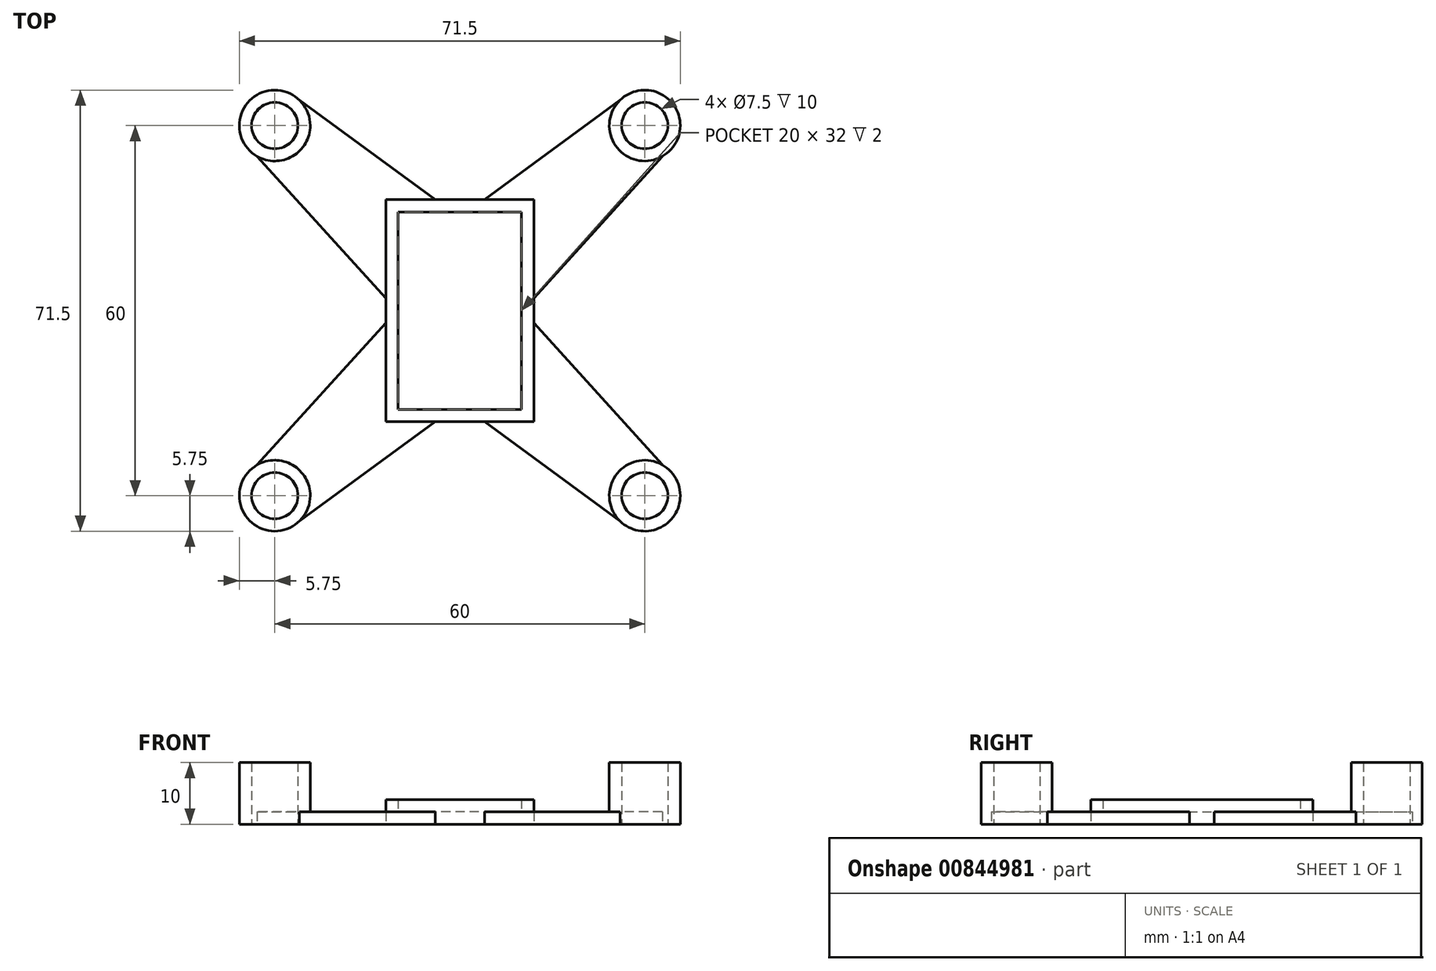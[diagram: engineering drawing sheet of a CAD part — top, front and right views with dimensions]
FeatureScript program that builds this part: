
annotation { "Feature Type Name" : "Feature", "Feature Type Description" : "" }
export const myFeature = defineFeature(function(context is Context, id is Id, definition is map)
    precondition{}
    {
        {
            var Q0;
            Q0=qCreatedBy(makeId("Top.planeOp"),FACE);
            var sketch = newSketch(context, id + "F0", { "sketchPlane" : qUnion([Q0])});
            skLineSegment(sketch, "E0.bottom", {"start": v(-30, 30) * mm, "end": v(30, 30) * mm, "construction": true});
            skLineSegment(sketch, "E0.top", {"start": v(-30, -30) * mm, "end": v(30, -30) * mm, "construction": true});
            skLineSegment(sketch, "E0.left", {"start": v(-30, 30) * mm, "end": v(-30, -30) * mm, "construction": true});
            skLineSegment(sketch, "E0.right", {"start": v(30, 30) * mm, "end": v(30, -30) * mm, "construction": true});
            skPoint(sketch, "E0.middle", {"position": v(0, 0) * mm});
            skCircle(sketch, "E1", {"center": v(-30, 30) * mm, "radius": 3.75 * mm});
            skCircle(sketch, "E2", {"center": v(30, 30) * mm, "radius": 3.75 * mm});
            skCircle(sketch, "E3", {"center": v(30, -30) * mm, "radius": 3.75 * mm});
            skCircle(sketch, "E4", {"center": v(-30, -30) * mm, "radius": 3.75 * mm});
            skLineSegment(sketch, "E5.bottom", {"start": v(-12, 18) * mm, "end": v(12, 18) * mm});
            skLineSegment(sketch, "E5.top", {"start": v(-12, -18) * mm, "end": v(12, -18) * mm});
            skLineSegment(sketch, "E5.left", {"start": v(-12, 18) * mm, "end": v(-12, -18) * mm});
            skLineSegment(sketch, "E5.right", {"start": v(12, 18) * mm, "end": v(12, -18) * mm});
            skCircle(sketch, "E6", {"center": v(-30, 30) * mm, "radius": 5.75 * mm});
            skLineSegment(sketch, "E7.bottom", {"start": v(-10, 16) * mm, "end": v(10, 16) * mm});
            skLineSegment(sketch, "E7.top", {"start": v(-10, -16) * mm, "end": v(10, -16) * mm});
            skLineSegment(sketch, "E7.left", {"start": v(-10, 16) * mm, "end": v(-10, -16) * mm});
            skLineSegment(sketch, "E7.right", {"start": v(10, 16) * mm, "end": v(10, -16) * mm});
            skCircle(sketch, "E8", {"center": v(-30, -30) * mm, "radius": 5.75 * mm});
            skCircle(sketch, "E9", {"center": v(30, -30) * mm, "radius": 5.75 * mm});
            skCircle(sketch, "E10", {"center": v(30, 30) * mm, "radius": 5.75 * mm});
            skLineSegment(sketch, "E11", {"start": v(-4, 18) * mm, "end": v(-26, 34.13) * mm});
            skLineSegment(sketch, "E12", {"start": v(-32.84, 25) * mm, "end": v(-12, 2) * mm});
            skLineSegment(sketch, "E13.MirrorCS", {"start": v(4, 18) * mm, "end": v(26, 34.13) * mm});
            skLineSegment(sketch, "E14.MirrorCS", {"start": v(32.84, 25) * mm, "end": v(12, 2) * mm});
            skLineSegment(sketch, "E15.MirrorCS", {"start": v(32.84, -25) * mm, "end": v(12, -2) * mm});
            skLineSegment(sketch, "E16.MirrorCS", {"start": v(4, -18) * mm, "end": v(26, -34.13) * mm});
            skLineSegment(sketch, "E17.MirrorCS", {"start": v(-32.84, -25) * mm, "end": v(-12, -2) * mm});
            skLineSegment(sketch, "E18.MirrorCS", {"start": v(-4, -18) * mm, "end": v(-26, -34.13) * mm});
            skSolve(sketch);
        }
        {
            var Q0;
            {var subQ0=sQuery(id+"F0.wireOp",EDGE,"E11");Q0=makeQuery(id+"F0.imprint","IMPRINT",FACE,{"disambiguationData":[TD([[makeQuery(id+"F0.imprint","IMPRINT",EDGE,{"derivedFrom":subQ0}),1.0]])]});}
            var Q1;
            {var subQ0=sQuery(id+"F0.wireOp",EDGE,"E13.MirrorCS");Q1=makeQuery(id+"F0.imprint","IMPRINT",FACE,{"disambiguationData":[TD([[makeQuery(id+"F0.imprint","IMPRINT",EDGE,{"derivedFrom":subQ0}),-1.0]])]});}
            var Q2;
            {var subQ0=sQuery(id+"F0.wireOp",EDGE,"E15.MirrorCS");Q2=makeQuery(id+"F0.imprint","IMPRINT",FACE,{"disambiguationData":[TD([[makeQuery(id+"F0.imprint","IMPRINT",EDGE,{"derivedFrom":subQ0}),1.0]])]});}
            var Q3;
            {var subQ0=sQuery(id+"F0.wireOp",EDGE,"E17.MirrorCS");Q3=makeQuery(id+"F0.imprint","IMPRINT",FACE,{"disambiguationData":[TD([[makeQuery(id+"F0.imprint","IMPRINT",EDGE,{"derivedFrom":subQ0}),-1.0]])]});}
            var Q4;
            Q4=makeQuery(id+"F0.imprint","IMPRINT",FACE,{"disambiguationData":[TD([[makeQuery(id+"F0.imprint","IMPRINT",EDGE,{"derivedFrom":sQuery(id+"F0.wireOp",EDGE,"E7.bottom")}),1.0]])]});
            var Q5;
            Q5=makeQuery(id+"F0.imprint","IMPRINT",FACE,{"disambiguationData":[TD([[makeQuery(id+"F0.imprint","IMPRINT",EDGE,{"derivedFrom":sQuery(id+"F0.wireOp",EDGE,"E7.bottom")}),-1.0]])]});
            extrude(context, id + "F1", {"entities" : qUnion([Q0, Q1, Q2, Q3, Q4, Q5]), "depth" : 2 * mm, "offsetDistance" : 25 * mm});
        }
        {
            var Q0;
            Q0=makeQuery(id+"F0.imprint","IMPRINT",FACE,{"disambiguationData":[TD([[makeQuery(id+"F0.imprint","IMPRINT",EDGE,{"derivedFrom":sQuery(id+"F0.wireOp",EDGE,"E7.bottom")}),1.0]])]});
            extrude(context, id + "F2", {"entities" : qUnion([Q0]), "operationType" : NewBodyOperationType.ADD, "depth" : 4 * mm, "offsetDistance" : 25 * mm});
        }
        {
            var Q0;
            Q0=makeQuery(id+"F0.imprint","IMPRINT",FACE,{"disambiguationData":[TD([[makeQuery(id+"F0.imprint","IMPRINT",EDGE,{"derivedFrom":sQuery(id+"F0.wireOp",EDGE,"E4")}),-1.0]])]});
            var Q1;
            Q1=makeQuery(id+"F0.imprint","IMPRINT",FACE,{"disambiguationData":[TD([[makeQuery(id+"F0.imprint","IMPRINT",EDGE,{"derivedFrom":sQuery(id+"F0.wireOp",EDGE,"E3")}),-1.0]])]});
            var Q2;
            Q2=makeQuery(id+"F0.imprint","IMPRINT",FACE,{"disambiguationData":[TD([[makeQuery(id+"F0.imprint","IMPRINT",EDGE,{"derivedFrom":sQuery(id+"F0.wireOp",EDGE,"E2")}),-1.0]])]});
            var Q3;
            Q3=makeQuery(id+"F0.imprint","IMPRINT",FACE,{"disambiguationData":[TD([[makeQuery(id+"F0.imprint","IMPRINT",EDGE,{"derivedFrom":sQuery(id+"F0.wireOp",EDGE,"E1")}),-1.0]])]});
            extrude(context, id + "F3", {"entities" : qUnion([Q0, Q1, Q2, Q3]), "operationType" : NewBodyOperationType.ADD, "depth" : 10 * mm, "offsetDistance" : 25 * mm});
        }
    });
